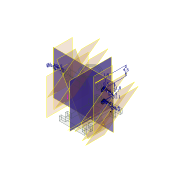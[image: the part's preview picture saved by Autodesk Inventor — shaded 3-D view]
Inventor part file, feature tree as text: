
AUTODESK INVENTOR PART (.ipt)
format: ipt  version: 2021 (Build 250183000, 183)  size: 338,944 bytes
history: native  units: in
note: dims shown in document units (in); Inventor stores cm internally (conversion verified against a paired STEP export)
features: plane x16, extrude x10, sketch x10, mirror x5, projected_geometry x4, revolve x3, split x2, fillet x2, boolean_combine x1
ambient origin geometry x8: Origin, YZ Plane, XZ Plane, XY Plane, X Axis, Y Axis, Z Axis, Center Point
bodies: Solid1 (feature_tree), Solid2 (feature_tree), Solid4 (feature_tree), Solid6 (feature_tree)
feature tree (53):
  extrude  "Extrusion1"  Depth=0.315in
  plane  "Work Plane1"
  sketch  "Sketch2"  dims[d2=0.748in d3=0.0in d4=0.2362in]
  extrude  "Extrusion2"  Depth=0.748in
  extrude  "Extrusion3"  Depth=0.0709in
  sketch  "Sketch3"  dims[d5=0.0709in d7=0.0709in]
  revolve  "Revolution1"  [1 undecoded]
  revolve  "Revolution3"  [1 undecoded]
  plane  "Work Plane2"
  plane  "Work Plane7"
  extrude  "Extrusion4"  Depth=0.0433in
  extrude  "Extrusion5"  Depth=0.0551in
  sketch  "Sketch6"  dims[d20=0.8268in d21=0.0in d23=0.0433in]
  revolve  "Revolution5"  [1 undecoded]
  plane  "Work Plane8"
  plane  "Work Plane9"
  plane  "Work Plane10"
  plane  "Work Plane15"
  split  "Split8"
  plane  "Work Plane16"
  split  "Split9"
  mirror  "Mirror1"
  mirror  "Mirror2"
  extrude  "Extrusion9"  TaperAngle=90.0deg  [1 undecoded]
  mirror  "Mirror3"
  extrude  "Extrusion13"  TaperAngle=30.0deg  [1 undecoded]
  extrude  "Extrusion14"  [1 undecoded]
  mirror  "Mirror4"
  mirror  "Mirror5"
  plane  "Work Plane21"
  extrude  "Extrusion15"  Depth=0.0512in
  extrude  "Extrusion16"  Depth=0.0512in
  fillet  "Fillet4"  Radius=0.0709in
  fillet  "Fillet5"  Radius=0.3937in
  boolean_combine  "Combine1"
  sketch  "Sketch1"  dims[d0=0.2354in d1=0.315in]
  sketch  "Sketch4"  dims[d9=0.1772in d14=0.8268in d15=0.0in]
  sketch  "Sketch5"  dims[d16=0.0197in d18=0.0197in]
  plane  "Work Plane11"
  plane  "Work Plane12"
  plane  "Work Plane13"
  sketch  "Sketch12"  dims[d30=0.0433in d34=0.0551in]
  plane  "Work Plane17"
  sketch  "Sketch16"  dims[d35=0.0433in d38=0.0551in]
  sketch  "Sketch17"  dims[d41=0.0433in d42=90.0deg]
  plane  "Work Plane18"
  plane  "Work Plane19"
  plane  "Work Plane20"
  sketch  "Sketch19"  dims[d44=90.0deg d46=30.0deg d51=-0.5118in d52=0.2756in d53=0.0709in d54=0.0709in d56=0.3937in d57=0.0in d58=0.0197in d59=0.0394in d60=0.3937in d61=0.0in d62=0.0433in d63=0.0551in d64=0.0433in d71=90.0deg d73=-0.2061in d74=-0.4173in d75=-0.5945in d81=0.3543in d82=0.1969in d104=0.2362in d105=0.1575in d106=0.0394in d107=0.0984in d108=0.0in d123=0.315in d124=0.7087in d125=0.0787in d126=0.0in d127=0.0394in d128=0.0787in d129=0.0394in d130=0.0787in d131=0.0in d132=-0.4331in d134=0.3937in d135=0.0in d136=0.2953in d137=0.0in d138=0.1378in d140=0.0512in d141=0.0197in d142=0.0118in d103=0.0197in]
  projected_geometry  "Project Cut Edges1"
  projected_geometry  "Project Cut Edges3"
  projected_geometry  "Project Cut Edges5"
  projected_geometry  "Project Cut Edges6"
note: 6 required parameter values undecoded (feature->parameter linkage not recoverable at this tier; creation-order binding heuristic only, values carry confidence <= 0.55)